# Revit family: Podajnik_recznikow_ZZ POP
name_source: partatom
category: Furniture
units: mm (PartAtom-declared; Revit-internal decimal feet)

## family parameters
Always vertical = Yes
Cut with Voids When Loaded = No
Host = Wall
Room Calculation Point = No
Shared = No

## types (1)
- Type 1
    Color / Kolor = Biały / Szary
    Depth / Glebokosc = 130 mm  [stored 0.426509 ft]
    Description = Podajnik ręczników ZZ POP, wykonany z plastiku ABS, cechuje atrakcyjny wygląd i staranne wykończenie. Jest bardzo łatwy w codziennym użytkowaniu. Wyjęcie z niego jednego papierowego lista powoduje wysunięcie się kolejnego. Podajnik pozwala na kontrolę poziomu ręczników, dzięki czemu wiadomo, kiedy dołożyć kolejną partię. Jest on zamykany na kluczyk. To pojemnik na ręczniki papierowe, który dzięki swej uniwersalności i atrakcyjnej cenie jest jednym z najczęściej wybieranych.
    Height / Wysokosc = 270 mm  [stored 0.885827 ft]
    Manufacturer = FANECO.com
    Manufacturer code / Kod producenta = 5901764290254
    Material finish / Wykonczenie = Plastic ABS
    Model = POP
    Product code / Kod produktu = P400PGWG
    URL = https://faneco.com
    Weight / Waga = 0.7 kg
    Width / Szerokosc = 270 mm  [stored 0.885827 ft]

note: [stored X ft] marks values corroborated as IEEE doubles in the binary element streams (Revit-internal decimal feet)

## geometry (parser evidence)
native form markers: Sweep x9
no freeform markers — native parametric forms only
